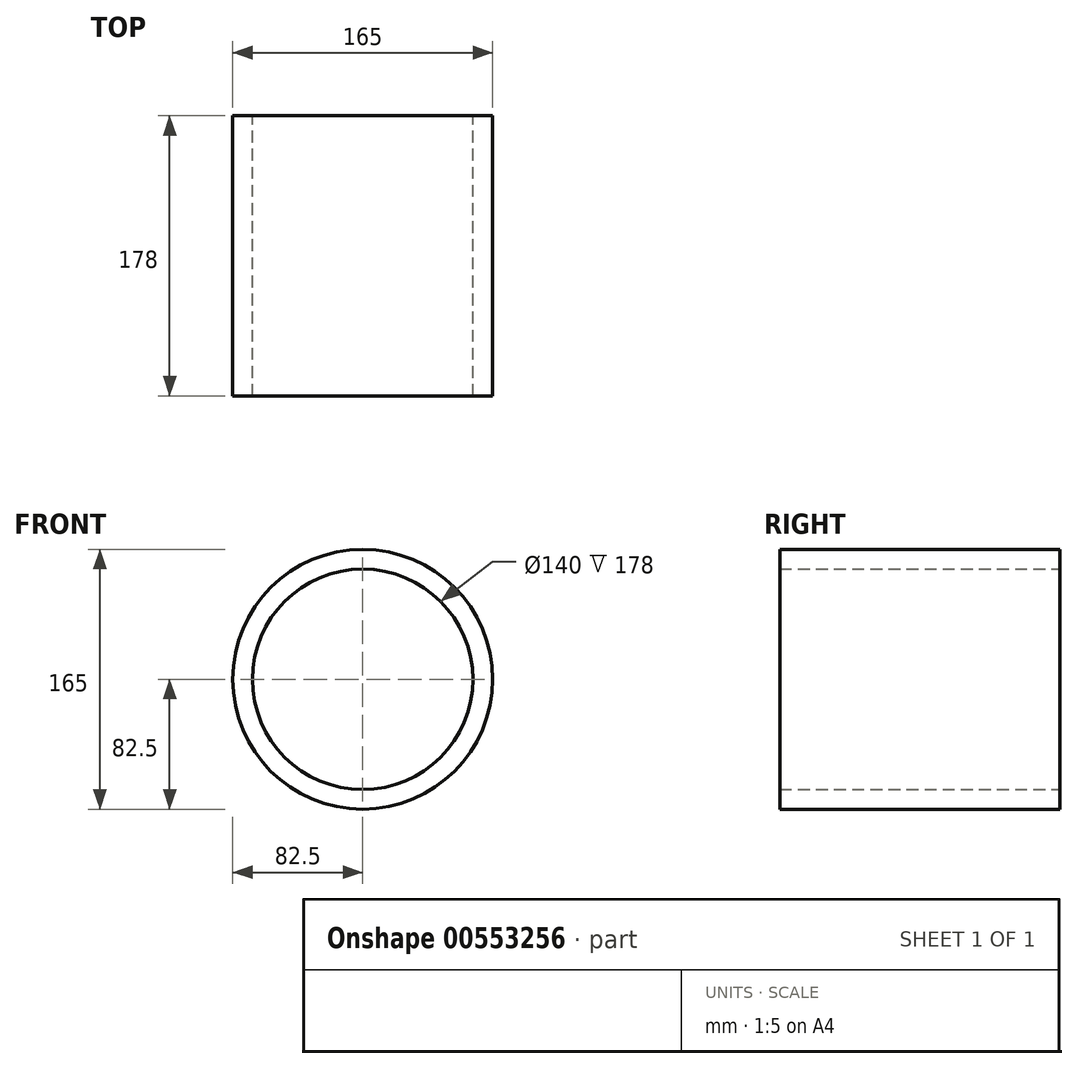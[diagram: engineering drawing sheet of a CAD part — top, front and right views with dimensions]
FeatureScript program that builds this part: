
annotation { "Feature Type Name" : "Feature", "Feature Type Description" : "" }
export const myFeature = defineFeature(function(context is Context, id is Id, definition is map)
    precondition{}
    {
        {
            var Q0;
            Q0=qCreatedBy(makeId("Front.planeOp"),FACE);
            var sketch = newSketch(context, id + "F0", { "sketchPlane" : qUnion([Q0])});
            skCircle(sketch, "E0", {"center": v(0, 0) * mm, "radius": 82.5 * mm});
            skCircle(sketch, "E1", {"center": v(0, 0) * mm, "radius": 70 * mm});
            skSolve(sketch);
        }
        {
            var Q0;
            Q0=makeQuery(id+"F0.imprint","IMPRINT",FACE,{"disambiguationData":[TD([[makeQuery(id+"F0.imprint","IMPRINT",EDGE,{"derivedFrom":sQuery(id+"F0.wireOp",EDGE,"E0")}),1.0]])]});
            extrude(context, id + "F1", {"entities" : qUnion([Q0]), "depth" : 178 * mm, "offsetDistance" : 25 * mm});
        }
    });
